# Revit family: LCOMN
name_source: partatom
category: Lighting Fixtures
units: mm (PartAtom-declared; Revit-internal decimal feet)

## family parameters
Cut with Voids When Loaded = No
Host = Face
Light Source = Yes
OmniClass Number = 23.80.70.11.14.11
OmniClass Title = Downlights
Part Type = Normal
Room Calculation Point = No
Round Connector Dimension = Use Diameter
Shared = No

## types (5) — shared parameters
Assembly Code = D5020200
Color Filter = 16777215
Default Elevation = 4' - 0"
Description = LED Commercial Type N
Dimming Lamp Color Temperature Shift = <None>
Housing Finish = Metal - Viscor - White
Lamp = LED
Lens Finish = Polycarbonate - Viscor - Frosted Round
Manufacturer = VISIONEERING by VISCOR
Model = LCOMN
Tilt Angle = -90.00°
URL = https://www.viscor.com
Voltage = 120 V
Width = 0' - 2 1/16"

## per-type parameters (varying)
| type | Apparent Load | Emit from Line Length | Lamp Wattage | Length | Photometric Web File |
| LCOMN24-LED840K020LUNV | 17 VA | 1' - 10 7/8" | 17 VA | 1' - 10 7/8" | LCOMN24-LED840K020LUNV-G0942.IES |
| LCOMN48-LED840K040LUNV | 34 VA | 3' - 8 7/8" | 34 VA | 3' - 8 7/8" | LCOMN48-LED840K040LUNV-G002026.IES |
| LCOMN48-LED840K020LUNV | 17 VA | 3' - 8 7/8" | 17 VA | 3' - 8 7/8" | LCOMN48-LED840K020LUNV-G0522.IES |
| LCOMN96-LED840K040LUNV | 34 VA | 7' - 5 1/4" | 34 VA | 7' - 5 1/4" | LCOMN96-LED840K040LUNV.ies |
| LCOMN96-LED840K080LUNV | 65 VA | 7' - 5 1/4" | 65 VA | 7' - 5 1/4" | LCOMN96-LED840K080LUNV.ies |

## geometry (parser evidence)
native form markers: Sweep x2
no freeform markers — native parametric forms only
